# Revit family: furniture feet 175_60, 2 pieces left
name_source: partatom
category: Furniture
units: mm (PartAtom-declared; Revit-internal decimal feet)

## family parameters
Always vertical = No
Cut with Voids When Loaded = No
OmniClass Number = 23.31.25.00
Room Calculation Point = No
Shared = Yes
Work Plane-Based = No

## types (6) — shared parameters
BASENUMBER = Furniture feet 175/60, left
BIMOBJECT = Furniture: Other Furniture
CATALOG = Hansgrohe
DESIGN = Germany
GTINCODE = 4059625458747
IFC = Furnishing element
MASTERFORMAT = 10 28 00 | Toilet, Bath, and Laundry Accessories
Manufacturer = Hansgrohe
NAME = Xelu Q Furniture feet 175/60, 2 pieces
NBSYN = $BASENUMBER.-$ARTNR.-$SURFACE.-$LODLEVEL.
NN = Furniture feet 175/60, 2 pieces Left
OBJECTTYPE = Object (single object)
OMNICLASS = 23-31 25 00 | Toilet and Bath Specialties
PERMALINK = 54145XXX
PRODUCTFAMILY = Xelu Q
PRODUCTGROUP = furniture feet
PRODUCTURL = https://pro.hansgrohe.com
REGIONSET = Worldwide
SPECIFICATION = Surfaces:    - 54145000 Chrome  - 54145670 Matt Black  - 54145700 Matt White      Specification:
UNIFORMATII = E2010 | Fixed Furnishings
UNSPSC = 301815 | Sanitary ware
WEIGHT = 0

## per-type parameters (varying)
| type | ARTNR | LINA | LODLEVEL | Model | NB | SURFACE |
| Furniture feet 175_60, left-54145000-CHROME-200 | 54145000 | Furniture feet 175/60, left-54145000-CHROME-200 | 200 | Furniture feet 175/60, left-54145000-CHROME-200 | Furniture feet 175/60, left-54145000-CHROME-200 | CHROME |
| Furniture feet 175_60, left-54145000-CHROME-400 | 54145000 | Furniture feet 175/60, left-54145000-CHROME-400 | 400 | Furniture feet 175/60, left-54145000-CHROME-400 | Furniture feet 175/60, left-54145000-CHROME-400 | CHROME |
| Furniture feet 175_60, left-54145670-MATT_BLACK-200 | 54145670 | Furniture feet 175/60, left-54145670-MATT_BLACK-200 | 200 | Furniture feet 175/60, left-54145670-MATT_BLACK-200 | Furniture feet 175/60, left-54145670-MATT_BLACK-200 | MATT_BLACK |
| Furniture feet 175_60, left-54145670-MATT_BLACK-400 | 54145670 | Furniture feet 175/60, left-54145670-MATT_BLACK-400 | 400 | Furniture feet 175/60, left-54145670-MATT_BLACK-400 | Furniture feet 175/60, left-54145670-MATT_BLACK-400 | MATT_BLACK |
| Furniture feet 175_60, left-54145700-MATT_WHITE-200 | 54145700 | Furniture feet 175/60, left-54145700-MATT_WHITE-200 | 200 | Furniture feet 175/60, left-54145700-MATT_WHITE-200 | Furniture feet 175/60, left-54145700-MATT_WHITE-200 | MATT_WHITE |
| Furniture feet 175_60, left-54145700-MATT_WHITE-400 | 54145700 | Furniture feet 175/60, left-54145700-MATT_WHITE-400 | 400 | Furniture feet 175/60, left-54145700-MATT_WHITE-400 | Furniture feet 175/60, left-54145700-MATT_WHITE-400 | MATT_WHITE |

type visibility flags: 6 boolean params named "<type name>_RX0RY0RZ0TX0TY0TZ0_V" — each type sets only its own to Yes (folded from table)

## geometry (parser evidence)
native form markers: Sweep x36
no freeform markers — native parametric forms only
